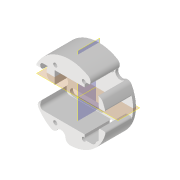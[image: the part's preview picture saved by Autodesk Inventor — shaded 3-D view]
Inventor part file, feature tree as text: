
AUTODESK INVENTOR PART (.ipt)
format: ipt  version: 2022 (Build 260153000, 153)  size: 327,680 bytes
history: native  units: in
note: dims shown in document units (in); Inventor stores cm internally (conversion verified against a paired STEP export)
features: other x8, sketch x8, extrude x7, fillet x5, reference x4, projected_geometry x3, plane x2, hole x1
ambient origin geometry x8: Origin, YZ Plane, XZ Plane, XY Plane, X Axis, Y Axis, Z Axis, Center Point
bodies: Solid2 (feature_tree)
feature tree (38):
  extrude  "Extrusion5"  Depth=0.0787in TaperAngle=0.0deg
  extrude  "Extrusion6"  Depth=0.7283in
  fillet  "Fillet2"  Radius=0.7283in
  extrude  "Extrusion7"  Depth=0.0787in TaperAngle=0.0deg
  hole  "Hole2"  [1 undecoded]
  plane  "Work Plane4"
  plane  "Work Plane5"
  fillet  "Fillet4"  Radius=0.0394in
  other  "Work Axis1"
  extrude  "Extrusion8"  Depth=0.3937in
  fillet  "Fillet5"  Radius=0.3937in
  extrude  "Extrusion9"  Depth=1.0in TaperAngle=0.0deg
  extrude  "Extrusion10"  Depth=0.125in
  fillet  "Fillet6"  Radius=0.2559in
  extrude  "Extrusion11"  Depth=0.125in
  fillet  "Fillet7"  Radius=0.2559in
  sketch  "Sketch6"  dims[d33=2.0472in d34=0.0787in d35=0.0in]
  sketch  "Sketch7"  dims[d36=1.6142in d37=1.122in d38=0.7283in d39=0.0in]
  sketch  "Sketch8"  dims[d40=0.0787in d41=0.4724in d42=0.0in]
  projected_geometry  "Projected Loop5"
  sketch  "Sketch9"  dims[d44=0.7874in d45=1.378in]
  projected_geometry  "Projected Loop6"
  sketch  "Sketch11"  dims[d46=0.1102in d47=0.75in d48=0.2559in d49=0.1181in d50=0.5635in d51=1.0in d52=0.8108in d53=0.0394in]
  projected_geometry  "Projected Loop7"
  sketch  "Sketch12"  dims[d57=0.0in d58=0.0in d59=0.7087in d60=0.3937in]
  reference  "Reference5"
  reference  "Reference6"
  reference  "Reference7"
  reference  "Reference8"
  sketch  "Sketch13"  dims[d61=0.1181in d62=1.0in d63=0.0in]
  sketch  "Sketch14"  dims[d64=1.0in d65=0.0in d66=0.1181in d67=0.2559in d68=0.2559in d69=0.2559in d70=1.0in d71=0.0in d72=0.125in]
  other  "<userpath>\Documents\MANATEE\INVENTOR\MANATEE_V1.iam"
  other  "MANATEE_V1.iam"
  other  "00_ESP3-CAM:1"
  other  "Pin Header 4 x 1 TH 2.54mm Pitch v1:1"
  other  "Pin Header 4 x 1 TH 2.54mm Pitch v1:2"
  other  "Pin Header 4 x 1 TH 2.54mm Pitch v1:3"
  other  "Pin Header 4 x 1 TH 2.54mm Pitch v1:4"
note: 1 required parameter value undecoded (feature->parameter linkage not recoverable at this tier; creation-order binding heuristic only, values carry confidence <= 0.55)
